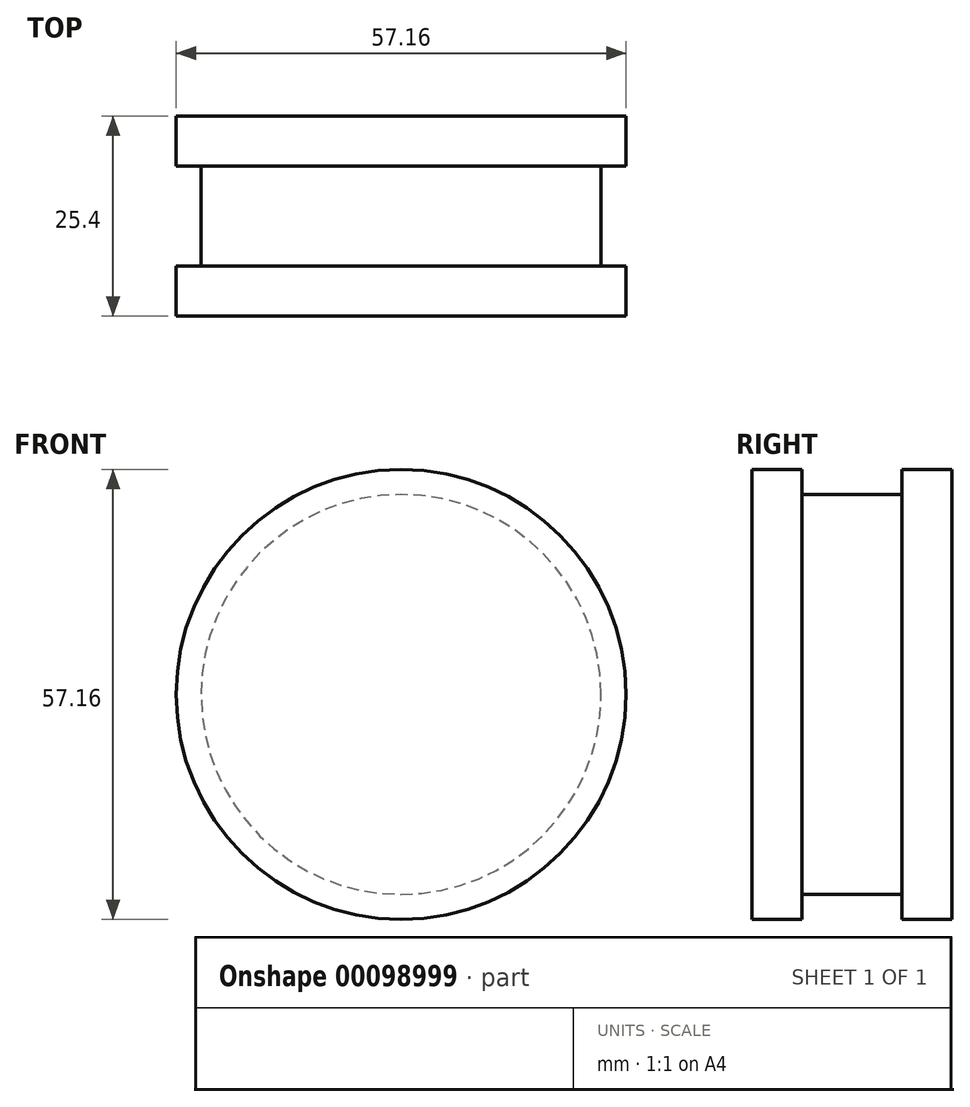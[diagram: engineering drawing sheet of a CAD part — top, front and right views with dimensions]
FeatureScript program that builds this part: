
annotation { "Feature Type Name" : "Feature", "Feature Type Description" : "" }
export const myFeature = defineFeature(function(context is Context, id is Id, definition is map)
    precondition{}
    {
        {
            var Q0;
            Q0=qCreatedBy(makeId("Front.planeOp"),FACE);
            var sketch = newSketch(context, id + "F0", { "sketchPlane" : qUnion([Q0])});
            skCircle(sketch, "E0", {"center": v(0, 0) * mm, "radius": 25.4 * mm});
            skSolve(sketch);
        }
        {
            var Q0;
            Q0=makeQuery(id+"F0.imprint","IMPRINT",FACE,{"disambiguationData":[TD([[makeQuery(id+"F0.imprint","IMPRINT",EDGE,{"derivedFrom":sQuery(id+"F0.wireOp",EDGE,"E0")}),1.0]])]});
            extrude(context, id + "F1", {"entities" : qUnion([Q0]), "depth" : 12.7 * mm});
        }
        {
            var Q0;
            Q0=makeQuery(id+"F1.opExtrude","CAP_FACE",FACE,{"disambiguationData":[OSD([sQuery(id+"F0.wireOp",EDGE,"E0")])],"isStart":false});
            var sketch = newSketch(context, id + "F2", { "sketchPlane" : qUnion([Q0])});
            skCircle(sketch, "E1", {"center": v(0, 0) * mm, "radius": 28.58 * mm});
            skSolve(sketch);
        }
        {
            var Q0;
            Q0 = qSketchRegion(id + "F2", true);
            extrude(context, id + "F3", {"entities" : qUnion([Q0]), "operationType" : NewBodyOperationType.ADD, "depth" : 6.35 * mm});
        }
        {
            var Q0;
            Q0=makeQuery(id+"F1.opExtrude","CAP_FACE",FACE,{"disambiguationData":[OSD([sQuery(id+"F0.wireOp",EDGE,"E0")])],"isStart":true});
            var sketch = newSketch(context, id + "F4", { "sketchPlane" : qUnion([Q0])});
            skCircle(sketch, "E2.0", {"center": v(0, 0) * mm, "radius": 28.58 * mm});
            skSolve(sketch);
        }
        {
            var Q0;
            Q0 = qSketchRegion(id + "F4", true);
            extrude(context, id + "F5", {"entities" : qUnion([Q0]), "operationType" : NewBodyOperationType.ADD, "depth" : 6.35 * mm});
        }
    });
